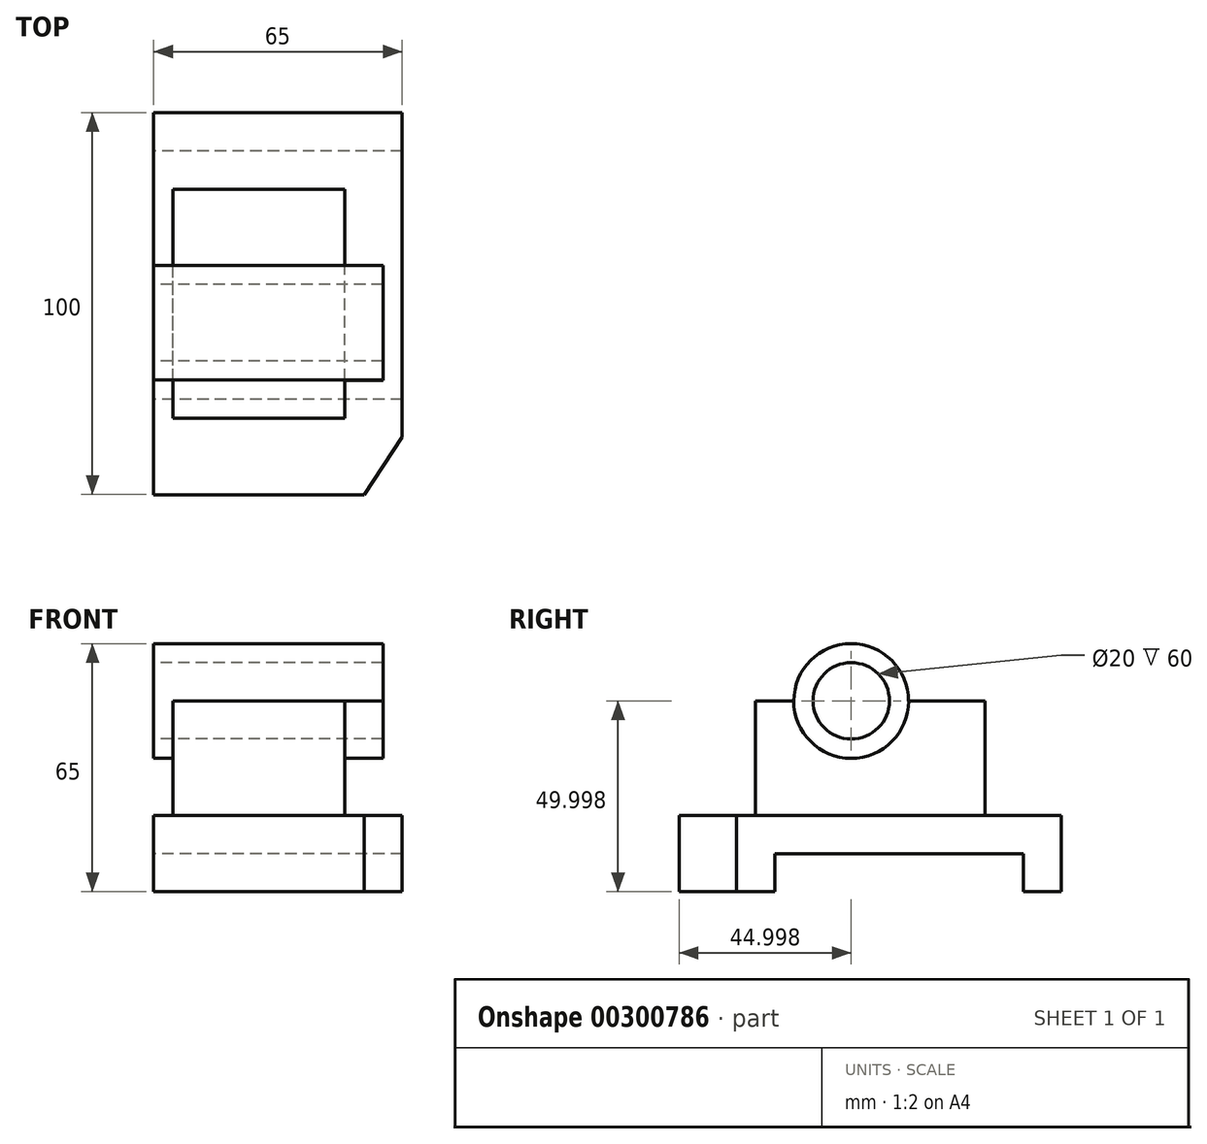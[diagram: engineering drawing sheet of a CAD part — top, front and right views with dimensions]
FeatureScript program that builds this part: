
annotation { "Feature Type Name" : "Feature", "Feature Type Description" : "" }
export const myFeature = defineFeature(function(context is Context, id is Id, definition is map)
    precondition{}
    {
        {
            var Q0;
            Q0=qCreatedBy(makeId("Right.planeOp"),FACE);
            var sketch = newSketch(context, id + "F0", { "sketchPlane" : qUnion([Q0])});
            skLineSegment(sketch, "E0.bottom", {"start": v(-51.07, 22.49) * mm, "end": v(48.93, 22.49) * mm});
            skLineSegment(sketch, "E0.top", {"start": v(-51.07, -27.51) * mm, "end": v(48.93, -27.51) * mm});
            skLineSegment(sketch, "E0.left", {"start": v(-51.07, 22.49) * mm, "end": v(-51.07, -27.51) * mm});
            skLineSegment(sketch, "E0.right", {"start": v(48.93, 22.49) * mm, "end": v(48.93, -27.51) * mm});
            skCircle(sketch, "E1", {"center": v(-6.07, 22.49) * mm, "radius": 10 * mm});
            skCircle(sketch, "E2", {"center": v(-6.07, 22.49) * mm, "radius": 15 * mm});
            skLineSegment(sketch, "E3.bottom", {"start": v(-31.07, 22.49) * mm, "end": v(28.93, 22.49) * mm});
            skLineSegment(sketch, "E3.top", {"start": v(-31.07, -7.51) * mm, "end": v(28.93, -7.51) * mm});
            skLineSegment(sketch, "E3.left", {"start": v(-31.07, 22.49) * mm, "end": v(-31.07, -7.51) * mm});
            skLineSegment(sketch, "E3.right", {"start": v(28.93, 22.49) * mm, "end": v(28.93, -7.51) * mm});
            skLineSegment(sketch, "E4.bottom", {"start": v(-26.07, -27.51) * mm, "end": v(38.93, -27.51) * mm});
            skLineSegment(sketch, "E4.top", {"start": v(-26.07, -17.51) * mm, "end": v(38.93, -17.51) * mm});
            skLineSegment(sketch, "E4.left", {"start": v(-26.07, -27.51) * mm, "end": v(-26.07, -17.51) * mm});
            skLineSegment(sketch, "E4.right", {"start": v(38.93, -27.51) * mm, "end": v(38.93, -17.51) * mm});
            skLineSegment(sketch, "E5", {"start": v(-31.07, -7.51) * mm, "end": v(-51.07, -7.51) * mm});
            skPoint(sketch, "E5.endSnap0", {"position": v(-51.07, -2.51) * mm});
            skLineSegment(sketch, "E6", {"start": v(28.93, -7.51) * mm, "end": v(48.93, -7.51) * mm});
            skSolve(sketch);
        }
        {
            var Q0;
            {var subQ0=sQuery(id+"F0.wireOp",EDGE,"E3.bottom");var subQ1=sQuery(id+"F0.wireOp",EDGE,"E1");var subQ2=makeQuery(id+"F0.imprint","INTERSECT",VERTEX,{"disambiguationData":[OD(0.0)],"derivedFrom":[subQ1,subQ0]});Q0=makeQuery(id+"F0.imprint","IMPRINT",FACE,{"disambiguationData":[TD([[makeQuery(id+"F0.imprint","IMPRINT",EDGE,{"disambiguationData":[TD([[subQ2,1.0]])],"derivedFrom":subQ1}),-1.0]])]});}
            var Q1;
            {var subQ0=sQuery(id+"F0.wireOp",EDGE,"E3.bottom");var subQ1=sQuery(id+"F0.wireOp",EDGE,"E1");var subQ2=makeQuery(id+"F0.imprint","INTERSECT",VERTEX,{"disambiguationData":[OD(0.0)],"derivedFrom":[subQ1,subQ0]});Q1=makeQuery(id+"F0.imprint","IMPRINT",FACE,{"disambiguationData":[TD([[makeQuery(id+"F0.imprint","IMPRINT",EDGE,{"disambiguationData":[TD([[subQ2,-1.0]])],"derivedFrom":subQ1}),-1.0]])]});}
            var Q2;
            Q2=makeQuery(id+"F0.imprint","IMPRINT",FACE,{"disambiguationData":[TD([[makeQuery(id+"F0.imprint","IMPRINT",EDGE,{"derivedFrom":sQuery(id+"F0.wireOp",EDGE,"E3.top")}),-1.0]])]});
            var Q3;
            Q3=makeQuery(id+"F0.imprint","IMPRINT",FACE,{"disambiguationData":[TD([[makeQuery(id+"F0.imprint","IMPRINT",EDGE,{"derivedFrom":sQuery(id+"F0.wireOp",EDGE,"E3.top")}),1.0]])]});
            extrude(context, id + "F1", {"entities" : qUnion([Q0, Q1, Q2, Q3]), "depth" : 65 * mm});
        }
        {
            var Q0;
            Q0=makeQuery(id+"F1.opExtrude","SWEPT_FACE",FACE,{"disambiguationData":[OSD([sQuery(id+"F0.wireOp",EDGE,"E5")])]});
            var sketch = newSketch(context, id + "F2", { "sketchPlane" : qUnion([Q0])});
            skLineSegment(sketch, "E7", {"start": v(65, -36.07) * mm, "end": v(55, -51.07) * mm});
            skSolve(sketch);
        }
        {
            var Q0;
            Q0 = qSketchRegion(id + "F2", true);
            var Q1;
            {var subQ0=sQuery(id+"F2.wireOp",EDGE,"E7");Q1=makeQuery(id+"F2.imprint","IMPRINT",FACE,{"disambiguationData":[TD([[makeQuery(id+"F2.imprint","IMPRINT",EDGE,{"derivedFrom":subQ0}),1.0]])]});}
            extrude(context, id + "F3", {"entities" : qUnion([Q0, Q1]), "operationType" : NewBodyOperationType.REMOVE, "oppositeDirection" : true, "depth" : 25 * mm});
        }
        {
            var Q0;
            Q0=makeQuery(id+"F1.opExtrude","CAP_FACE",FACE,{"disambiguationData":[OSD([sQuery(id+"F0.wireOp",EDGE,"E0.top"),sQuery(id+"F0.wireOp",EDGE,"E0.left"),sQuery(id+"F0.wireOp",EDGE,"E0.right"),sQuery(id+"F0.wireOp",EDGE,"E1"),sQuery(id+"F0.wireOp",EDGE,"E2"),sQuery(id+"F0.wireOp",EDGE,"E3.bottom"),sQuery(id+"F0.wireOp",EDGE,"E3.left"),sQuery(id+"F0.wireOp",EDGE,"E3.right"),sQuery(id+"F0.wireOp",EDGE,"E4.top"),sQuery(id+"F0.wireOp",EDGE,"E4.left"),sQuery(id+"F0.wireOp",EDGE,"E4.right"),sQuery(id+"F0.wireOp",EDGE,"E5"),sQuery(id+"F0.wireOp",EDGE,"E6")])],"isStart":false});
            var sketch = newSketch(context, id + "F4", { "sketchPlane" : qUnion([Q0])});
            skLineSegment(sketch, "E8", {"start": v(-31.07, -7.51) * mm, "end": v(28.93, -7.51) * mm});
            skSolve(sketch);
        }
        {
            var Q0;
            Q0=makeQuery(id+"F4.imprint","IMPRINT",FACE,{"disambiguationData":[TD([[makeQuery(id+"F4.imprint","IMPRINT",EDGE,{"derivedFrom":sQuery(id+"F4.wireOp",EDGE,"E8")}),1.0]])]});
            extrude(context, id + "F5", {"entities" : qUnion([Q0]), "operationType" : NewBodyOperationType.REMOVE, "oppositeDirection" : true, "depth" : 5 * mm});
        }
        {
            var Q0;
            Q0=makeQuery(id+"F5.boolean.opBoolean","COPY",FACE,{"derivedFrom":makeQuery(id+"F5.opExtrude","CAP_FACE",FACE,{"disambiguationData":[OSD([sQuery(id+"F0.wireOp",EDGE,"E1"),sQuery(id+"F0.wireOp",EDGE,"E2"),sQuery(id+"F0.wireOp",EDGE,"E3.bottom"),sQuery(id+"F0.wireOp",EDGE,"E3.left"),sQuery(id+"F0.wireOp",EDGE,"E3.right"),sQuery(id+"F4.wireOp",EDGE,"E8")])],"isStart":false})});
            var sketch = newSketch(context, id + "F6", { "sketchPlane" : qUnion([Q0])});
            skCircle(sketch, "E9", {"center": v(-6.07, 22.49) * mm, "radius": 15.05 * mm});
            skSolve(sketch);
        }
        {
            var Q0;
            Q0=makeQuery(id+"F6.imprint","IMPRINT",FACE,{"disambiguationData":[TD([[makeQuery(id+"F6.imprint","IMPRINT",EDGE,{"derivedFrom":makeQuery(id+"F5.boolean.opBoolean","COPY",EDGE,{"derivedFrom":makeQuery(id+"F5.opExtrude","CAP_EDGE",EDGE,{"disambiguationData":[OSD([sQuery(id+"F4.wireOp",EDGE,"E8")])],"isStart":false})})}),1.0]])]});
            extrude(context, id + "F7", {"entities" : qUnion([Q0]), "operationType" : NewBodyOperationType.REMOVE, "oppositeDirection" : true, "depth" : 10 * mm});
        }
        {
            var Q0;
            Q0=makeQuery(id+"F0.imprint","IMPRINT",FACE,{"disambiguationData":[TD([[makeQuery(id+"F0.imprint","IMPRINT",EDGE,{"derivedFrom":sQuery(id+"F0.wireOp",EDGE,"E3.top")}),1.0]])]});
            extrude(context, id + "F8", {"entities" : qUnion([Q0]), "operationType" : NewBodyOperationType.REMOVE, "depth" : 5 * mm});
        }
    });
